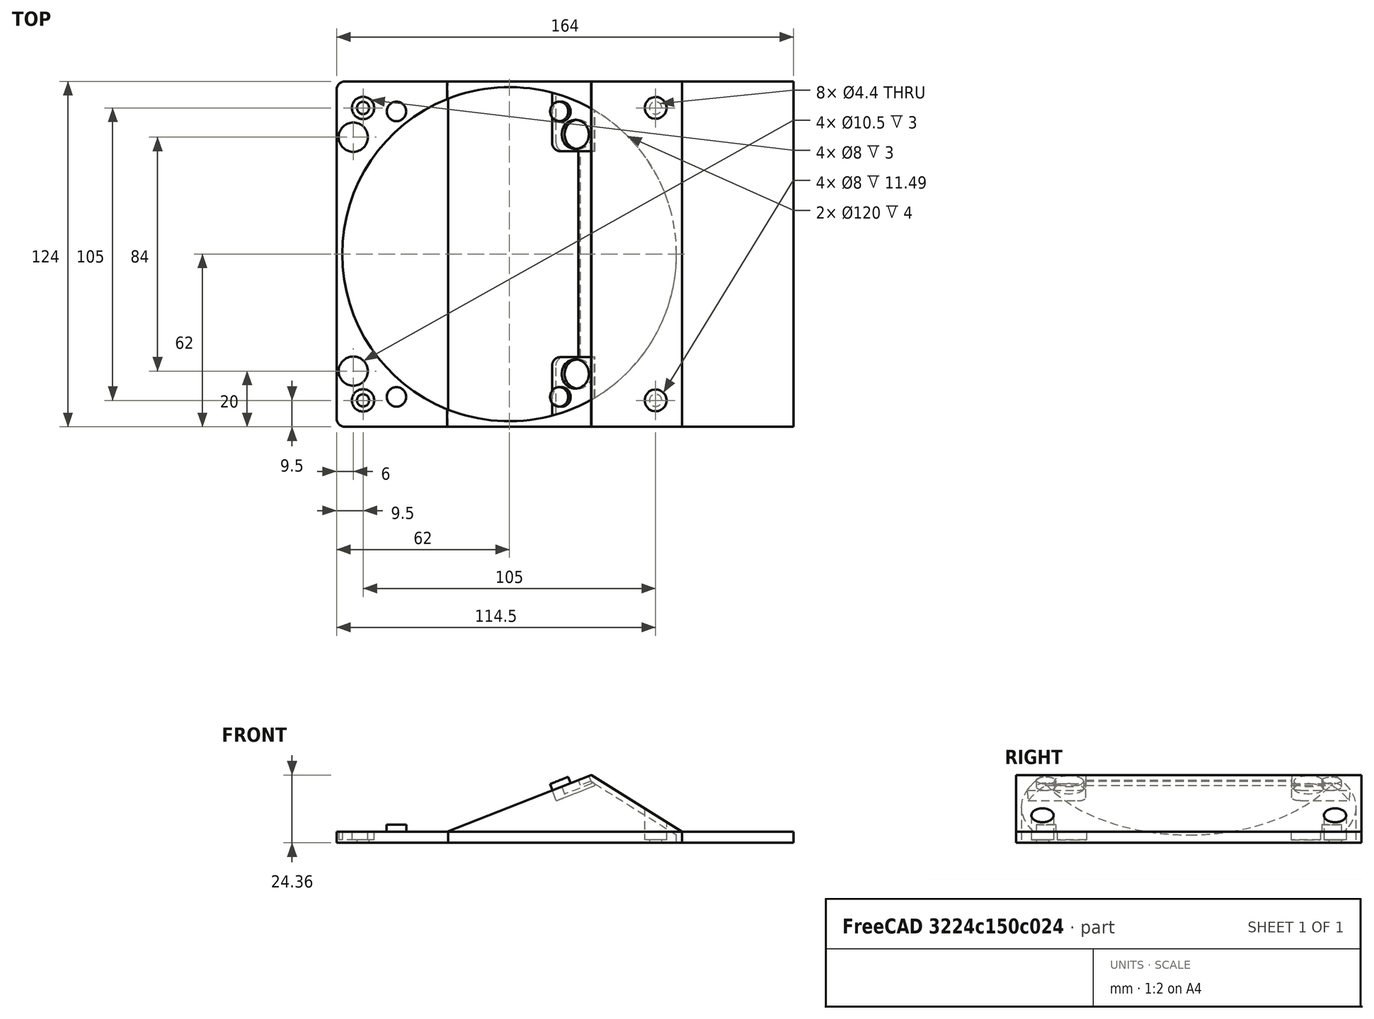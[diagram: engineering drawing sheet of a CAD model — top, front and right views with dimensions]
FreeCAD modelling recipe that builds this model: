
FCSTD DOCUMENT  (FreeCAD 0.20R29603 (Git))
Label: victron_fan_holder_mp2_8000
License: Creative Commons Attribution-NonCommercial-ShareAlike
LicenseURL: http://creativecommons.org/licenses/by-nc-sa/4.0/
objects: Part::Cylinder×39, Part::Cut×36, Part::Box×17, Part::MultiFuse×12, Part::Fillet×6
note: 110 computed .brp shape members not serialized (recipe doc carries the construction recipe); baked Part::Feature solids carry a one-line shape summary decoded from their .brp

FEATURE [Part::Cylinder] Cylinder
  Angle = 360
  AttacherType = Attacher::AttachEngine3D
  FirstAngle = 0
  Height = 4
  Placement = pos=(0,0,-4) rot=(0,0,1;0rad)
  Radius = 60
  SecondAngle = 0
FEATURE [Part::Box] Box  label="Cube"
  AttacherType = Attacher::AttachEngine3D
  Height = 4
  Length = 124
  Placement = pos=(-62,-62,-4) rot=(0,0,1;0rad)
  Width = 124
FEATURE [Part::Cylinder] Cylinder001  label="magnet_hole_1"
  Angle = 360
  AttacherType = Attacher::AttachEngine3D
  FirstAngle = 0
  Height = 3
  Placement = pos=(-56,-42,-3) rot=(0,0,1;0rad)
  Radius = 5.25
  SecondAngle = 0
FEATURE [Part::Cut] Cut
  Base = -> Box
  Tool = -> Cylinder
FEATURE [Part::Cylinder] Cylinder002  label="fan_hole_1"
  Angle = 360
  AttacherType = Attacher::AttachEngine3D
  FirstAngle = 0
  Height = 4
  Placement = pos=(-52.5,-52.5,-4) rot=(0,0,1;0rad)
  Radius = 2.2
  SecondAngle = 0
FEATURE [Part::Cylinder] Cylinder003  label="fan_hole_1_deepening"
  Angle = 360
  AttacherType = Attacher::AttachEngine3D
  FirstAngle = 0
  Height = 3
  Placement = pos=(-52.5,-52.5,-3) rot=(0,0,1;0rad)
  Radius = 4
  SecondAngle = 0
FEATURE [Part::Cylinder] Cylinder004  label="fan_hole_2_deepening"
  Angle = 360
  AttacherType = Attacher::AttachEngine3D
  FirstAngle = 0
  Height = 50
  Placement = pos=(52.5,-52.5,-3) rot=(0,0,1;0rad)
  Radius = 4
  SecondAngle = 0
FEATURE [Part::Cylinder] Cylinder005  label="fan_hole_2"
  Angle = 360
  AttacherType = Attacher::AttachEngine3D
  FirstAngle = 0
  Height = 50
  Placement = pos=(52.5,-52.5,-4) rot=(0,0,1;0rad)
  Radius = 2.2
  SecondAngle = 0
FEATURE [Part::Cylinder] Cylinder006  label="fan_hole_3_deepening"
  Angle = 360
  AttacherType = Attacher::AttachEngine3D
  FirstAngle = 0
  Height = 3
  Placement = pos=(-52.5,52.5,-3) rot=(0,0,1;0rad)
  Radius = 4
  SecondAngle = 0
FEATURE [Part::Cylinder] Cylinder007  label="fan_hole_3"
  Angle = 360
  AttacherType = Attacher::AttachEngine3D
  FirstAngle = 0
  Height = 4
  Placement = pos=(-52.5,52.5,-4) rot=(0,0,1;0rad)
  Radius = 2.2
  SecondAngle = 0
FEATURE [Part::Cylinder] Cylinder008  label="fan_hole_4_deepening"
  Angle = 360
  AttacherType = Attacher::AttachEngine3D
  FirstAngle = 0
  Height = 50
  Placement = pos=(52.5,52.5,-3) rot=(0,0,1;0rad)
  Radius = 4
  SecondAngle = 0
FEATURE [Part::Cylinder] Cylinder009  label="fan_hole_4"
  Angle = 360
  AttacherType = Attacher::AttachEngine3D
  FirstAngle = 0
  Height = 50
  Placement = pos=(52.5,52.5,-4) rot=(0,0,1;0rad)
  Radius = 2.2
  SecondAngle = 0
FEATURE [Part::Cylinder] Cylinder010  label="pin_1"
  Angle = 360
  AttacherType = Attacher::AttachEngine3D
  FirstAngle = 0
  Height = 2.5
  Placement = pos=(-40.5,-51.25,0) rot=(0,0,1;0rad)
  Radius = 3.5
  SecondAngle = 0
FEATURE [Part::Cylinder] Cylinder011  label="pin_2"
  Angle = 360
  AttacherType = Attacher::AttachEngine3D
  FirstAngle = 0
  Height = 2.5
  Placement = pos=(-40.5,51.25,0) rot=(0,0,1;0rad)
  Radius = 3.5
  SecondAngle = 0
FEATURE [Part::Box] Box002  label="Cube002"
  AttacherType = Attacher::AttachEngine3D
  Height = 50
  Length = 83
  Placement = pos=(-9,-62,-48.5) rot=(0,-1,0;0.375246rad)
  Width = 124
FEATURE [Part::Cylinder] Cylinder012  label="magnet_hole_2"
  Angle = 360
  AttacherType = Attacher::AttachEngine3D
  FirstAngle = 0
  Height = 3
  Placement = pos=(-56,42,-3) rot=(0,0,1;0rad)
  Radius = 5.25
  SecondAngle = 0
FEATURE [Part::Cylinder] Cylinder013
  Angle = 360
  AttacherType = Attacher::AttachEngine3D
  FirstAngle = 0
  Height = 100
  Placement = pos=(0,0,-4) rot=(0,0,1;0rad)
  Radius = 60
  SecondAngle = 0
FEATURE [Part::Box] Box003  label="Cube003"
  AttacherType = Attacher::AttachEngine3D
  Height = 4
  Length = 124
  Placement = pos=(-22,-62,-4) rot=(0,0,1;0rad)
  Width = 124
FEATURE [Part::Box] Box004  label="rear_slant"
  AttacherType = Attacher::AttachEngine3D
  Height = 2
  Length = 38.5
  Placement = pos=(28.3,-62,18.65) rot=(0,1,0;0.558505rad)
  Width = 124
FEATURE [Part::Cut] Cut001
  Base = -> Box002
  Tool = -> Cylinder013
FEATURE [Part::Box] Box007  label="Cube007"
  AttacherType = Attacher::AttachEngine3D
  Height = 100
  Length = 200
  Placement = pos=(-100,-100,-100) rot=(0,0,1;0rad)
  Width = 200
FEATURE [Part::Cut] Cut002
  Base = -> Cut001
  Tool = -> Box007
FEATURE [Part::Cylinder] Cylinder014  label="pin_003"
  Angle = 360
  AttacherType = Attacher::AttachEngine3D
  FirstAngle = 0
  Height = 2.5
  Placement = pos=(18.8026,-51.25,16.0727) rot=(0,-1,0;0.375246rad)
  Radius = 3.5
  SecondAngle = 0
FEATURE [Part::Box] Box008  label="pinholder_3"
  AttacherType = Attacher::AttachEngine3D
  Height = 4
  Length = 15
  Placement = pos=(16.8,-62,11.1) rot=(0,-1,0;0.375246rad)
  Width = 25
FEATURE [Part::Cylinder] Cylinder015  label="magnet_hole_003"
  Angle = 360
  AttacherType = Attacher::AttachEngine3D
  FirstAngle = 0
  Height = 3
  Placement = pos=(24.73,-43,15.4) rot=(0,-1,0;0.375246rad)
  Radius = 5.25
  SecondAngle = 0
FEATURE [Part::Box] Box009  label="pinholder_4"
  AttacherType = Attacher::AttachEngine3D
  Height = 4
  Length = 15
  Placement = pos=(16.8,37,11.1) rot=(0,-1,0;0.375246rad)
  Width = 25
FEATURE [Part::Cylinder] Cylinder016  label="pin_004"
  Angle = 360
  AttacherType = Attacher::AttachEngine3D
  FirstAngle = 0
  Height = 2.5
  Placement = pos=(18.8,51.25,16.07) rot=(0,-1,0;0.375246rad)
  Radius = 3.5
  SecondAngle = 0
FEATURE [Part::Fillet] Fillet
  Base = -> Cut
  Edges = 2 edges r=3: [Edge1,Edge3]
FEATURE [Part::Fillet] Fillet001
  Base = -> Box008
  Edges = 1 edges r=3: [Edge3]
FEATURE [Part::Fillet] Fillet002
  Base = -> Box009
  Edges = 1 edges r=3: [Edge1]
FEATURE [Part::MultiFuse] Fusion
  Shapes = -> [Fillet,Cylinder010,Cylinder011]
FEATURE [Part::Cut] Cut003
  Base = -> Fusion
  Tool = -> Cylinder001
FEATURE [Part::Cut] Cut004
  Base = -> Cut003
  Tool = -> Cylinder012
FEATURE [Part::Cut] Cut005
  Base = -> Cut004
  Tool = -> Cylinder002
FEATURE [Part::Cut] Cut006
  Base = -> Cut005
  Tool = -> Cylinder003
FEATURE [Part::Cut] Cut007
  Base = -> Cut006
  Tool = -> Cylinder006
FEATURE [Part::Cut] Cut008
  Base = -> Cut007
  Tool = -> Cylinder007
FEATURE [Part::MultiFuse] Fusion001
  Shapes = -> [Cut008,Cut002]
FEATURE [Part::Box] Box010  label="Cube010"
  AttacherType = Attacher::AttachEngine3D
  Height = 20
  Length = 57
  Placement = pos=(13,-62,30.5) rot=(0,1,0;0.558505rad)
  Width = 124
FEATURE [Part::Cut] Cut009
  Base = -> Fusion001
  Tool = -> Box010
FEATURE [Part::MultiFuse] Fusion002
  Shapes = -> [Cut009,Box004]
FEATURE [Part::MultiFuse] Fusion003
  Shapes = -> [Fusion002,Fillet002,Fillet001]
FEATURE [Part::MultiFuse] Fusion004
  Shapes = -> [Fusion003,Cylinder016,Cylinder014]
FEATURE [Part::Box] Box011  label="pinholder_004"
  AttacherType = Attacher::AttachEngine3D
  Height = 2
  Length = 5
  Placement = pos=(25.5042,-62,16.665) rot=(0,-1,0;0.375246rad)
  Width = 124
FEATURE [Part::Cylinder] Cylinder017  label="magnet_hole_004"
  Angle = 360
  AttacherType = Attacher::AttachEngine3D
  FirstAngle = 0
  Height = 3
  Placement = pos=(24.73,43,15.4) rot=(0,-1,0;0.375246rad)
  Radius = 5.25
  SecondAngle = 0
FEATURE [Part::Cut] Cut010
  Base = -> Fusion004
  Tool = -> Cylinder017
FEATURE [Part::Cut] Cut011
  Base = -> Cut010
  Tool = -> Cylinder015
FEATURE [Part::Cut] Cut012
  Base = -> Cut011
  Tool = -> Cylinder009
FEATURE [Part::Cut] Cut013
  Base = -> Cut012
  Tool = -> Cylinder008
FEATURE [Part::Cut] Cut014
  Base = -> Cut013
  Tool = -> Cylinder005
FEATURE [Part::Cut] Cut015
  Base = -> Cut014
  Tool = -> Cylinder004
FEATURE [Part::Cylinder] Cylinder018  label="magnet_hole_005"
  Angle = 360
  AttacherType = Attacher::AttachEngine3D
  FirstAngle = 0
  Height = 3
  Placement = pos=(24.73,-43,15.4) rot=(0,-1,0;0.375246rad)
  Radius = 5.25
  SecondAngle = 0
FEATURE [Part::Cut] Cut016
  Base = -> Box011
  Tool = -> Cylinder018
FEATURE [Part::Cylinder] Cylinder019  label="magnet_hole_006"
  Angle = 360
  AttacherType = Attacher::AttachEngine3D
  FirstAngle = 0
  Height = 3
  Placement = pos=(24.73,43,15.4) rot=(0,-1,0;0.375246rad)
  Radius = 5.25
  SecondAngle = 0
FEATURE [Part::Cut] Cut017
  Base = -> Cut016
  Tool = -> Cylinder019
FEATURE [Part::MultiFuse] Fusion005  label="fan_holder_l"
  Shapes = -> [Cut017,Cut015]
FEATURE [Part::Box] Box012  label="Cube011"
  AttacherType = Attacher::AttachEngine3D
  Height = 4
  Length = 124
  Placement = pos=(-62,-62,-4) rot=(0,0,1;0rad)
  Width = 124
FEATURE [Part::Box] Box013  label="Cube012"
  AttacherType = Attacher::AttachEngine3D
  Height = 50
  Length = 83
  Placement = pos=(-9,-62,-48.5) rot=(0,-1,0;0.375246rad)
  Width = 124
FEATURE [Part::Box] Box014  label="rear_slant001"
  AttacherType = Attacher::AttachEngine3D
  Height = 2
  Length = 38.5
  Placement = pos=(28.3,-62,18.65) rot=(0,1,0;0.558505rad)
  Width = 124
FEATURE [Part::Box] Box015  label="Cube013"
  AttacherType = Attacher::AttachEngine3D
  Height = 100
  Length = 200
  Placement = pos=(-100,-100,-100) rot=(0,0,1;0rad)
  Width = 200
FEATURE [Part::Box] Box016  label="pinholder_005"
  AttacherType = Attacher::AttachEngine3D
  Height = 4
  Length = 15
  Placement = pos=(16.8,-62,11.1) rot=(0,-1,0;0.375246rad)
  Width = 25
FEATURE [Part::Box] Box017  label="pinholder_006"
  AttacherType = Attacher::AttachEngine3D
  Height = 4
  Length = 15
  Placement = pos=(16.8,37,11.1) rot=(0,-1,0;0.375246rad)
  Width = 25
FEATURE [Part::Box] Box018  label="Cube014"
  AttacherType = Attacher::AttachEngine3D
  Height = 20
  Length = 57
  Placement = pos=(13,-62,30.5) rot=(0,1,0;0.558505rad)
  Width = 124
FEATURE [Part::Box] Box019  label="pinholder_007"
  AttacherType = Attacher::AttachEngine3D
  Height = 2
  Length = 5
  Placement = pos=(25.5042,-62,16.665) rot=(0,-1,0;0.375246rad)
  Width = 124
FEATURE [Part::Cylinder] Cylinder020
  Angle = 360
  AttacherType = Attacher::AttachEngine3D
  FirstAngle = 0
  Height = 4
  Placement = pos=(0,0,-4) rot=(0,0,1;0rad)
  Radius = 60
  SecondAngle = 0
FEATURE [Part::Cut] Cut018
  Base = -> Box012
  Tool = -> Cylinder020
FEATURE [Part::Cylinder] Cylinder021  label="magnet_hole_007"
  Angle = 360
  AttacherType = Attacher::AttachEngine3D
  FirstAngle = 0
  Height = 3
  Placement = pos=(-56,-42,-3) rot=(0,0,1;0rad)
  Radius = 5.25
  SecondAngle = 0
FEATURE [Part::Cylinder] Cylinder022  label="fan_hole_005"
  Angle = 360
  AttacherType = Attacher::AttachEngine3D
  FirstAngle = 0
  Height = 4
  Placement = pos=(-52.5,-52.5,-4) rot=(0,0,1;0rad)
  Radius = 2.2
  SecondAngle = 0
FEATURE [Part::Cylinder] Cylinder023  label="fan_hole_1_deepening001"
  Angle = 360
  AttacherType = Attacher::AttachEngine3D
  FirstAngle = 0
  Height = 3
  Placement = pos=(-52.5,-52.5,-3) rot=(0,0,1;0rad)
  Radius = 4
  SecondAngle = 0
FEATURE [Part::Cylinder] Cylinder024  label="fan_hole_2_deepening001"
  Angle = 360
  AttacherType = Attacher::AttachEngine3D
  FirstAngle = 0
  Height = 50
  Placement = pos=(52.5,-52.5,-3) rot=(0,0,1;0rad)
  Radius = 4
  SecondAngle = 0
FEATURE [Part::Cylinder] Cylinder025  label="fan_hole_006"
  Angle = 360
  AttacherType = Attacher::AttachEngine3D
  FirstAngle = 0
  Height = 50
  Placement = pos=(52.5,-52.5,-4) rot=(0,0,1;0rad)
  Radius = 2.2
  SecondAngle = 0
FEATURE [Part::Cylinder] Cylinder026  label="fan_hole_3_deepening001"
  Angle = 360
  AttacherType = Attacher::AttachEngine3D
  FirstAngle = 0
  Height = 3
  Placement = pos=(-52.5,52.5,-3) rot=(0,0,1;0rad)
  Radius = 4
  SecondAngle = 0
FEATURE [Part::Cylinder] Cylinder027  label="fan_hole_007"
  Angle = 360
  AttacherType = Attacher::AttachEngine3D
  FirstAngle = 0
  Height = 4
  Placement = pos=(-52.5,52.5,-4) rot=(0,0,1;0rad)
  Radius = 2.2
  SecondAngle = 0
FEATURE [Part::Cylinder] Cylinder028  label="fan_hole_4_deepening001"
  Angle = 360
  AttacherType = Attacher::AttachEngine3D
  FirstAngle = 0
  Height = 50
  Placement = pos=(52.5,52.5,-3) rot=(0,0,1;0rad)
  Radius = 4
  SecondAngle = 0
FEATURE [Part::Cylinder] Cylinder029  label="fan_hole_008"
  Angle = 360
  AttacherType = Attacher::AttachEngine3D
  FirstAngle = 0
  Height = 50
  Placement = pos=(52.5,52.5,-4) rot=(0,0,1;0rad)
  Radius = 2.2
  SecondAngle = 0
FEATURE [Part::Cylinder] Cylinder030  label="pin_005"
  Angle = 360
  AttacherType = Attacher::AttachEngine3D
  FirstAngle = 0
  Height = 2.5
  Placement = pos=(-40.5,-51.25,0) rot=(0,0,1;0rad)
  Radius = 3.5
  SecondAngle = 0
FEATURE [Part::Cylinder] Cylinder032  label="magnet_hole_008"
  Angle = 360
  AttacherType = Attacher::AttachEngine3D
  FirstAngle = 0
  Height = 3
  Placement = pos=(-56,42,-3) rot=(0,0,1;0rad)
  Radius = 5.25
  SecondAngle = 0
FEATURE [Part::Cylinder] Cylinder033
  Angle = 360
  AttacherType = Attacher::AttachEngine3D
  FirstAngle = 0
  Height = 100
  Placement = pos=(0,0,-4) rot=(0,0,1;0rad)
  Radius = 60
  SecondAngle = 0
FEATURE [Part::Cut] Cut019
  Base = -> Box013
  Tool = -> Cylinder033
FEATURE [Part::Cut] Cut020
  Base = -> Cut019
  Tool = -> Box015
FEATURE [Part::Cylinder] Cylinder034  label="pin_007"
  Angle = 360
  AttacherType = Attacher::AttachEngine3D
  FirstAngle = 0
  Height = 2.5
  Placement = pos=(18.8026,-51.25,16.0727) rot=(0,-1,0;0.375246rad)
  Radius = 3.5
  SecondAngle = 0
FEATURE [Part::Cylinder] Cylinder035  label="magnet_hole_009"
  Angle = 360
  AttacherType = Attacher::AttachEngine3D
  FirstAngle = 0
  Height = 3
  Placement = pos=(24.73,-43,15.4) rot=(0,-1,0;0.375246rad)
  Radius = 5.25
  SecondAngle = 0
FEATURE [Part::Cylinder] Cylinder036  label="pin_008"
  Angle = 360
  AttacherType = Attacher::AttachEngine3D
  FirstAngle = 0
  Height = 2.5
  Placement = pos=(18.8,51.25,16.07) rot=(0,-1,0;0.375246rad)
  Radius = 3.5
  SecondAngle = 0
FEATURE [Part::Cylinder] Cylinder037  label="magnet_hole_010"
  Angle = 360
  AttacherType = Attacher::AttachEngine3D
  FirstAngle = 0
  Height = 3
  Placement = pos=(24.73,43,15.4) rot=(0,-1,0;0.375246rad)
  Radius = 5.25
  SecondAngle = 0
FEATURE [Part::Cylinder] Cylinder038  label="magnet_hole_011"
  Angle = 360
  AttacherType = Attacher::AttachEngine3D
  FirstAngle = 0
  Height = 3
  Placement = pos=(24.73,-43,15.4) rot=(0,-1,0;0.375246rad)
  Radius = 5.25
  SecondAngle = 0
FEATURE [Part::Cut] Cut034
  Base = -> Box019
  Tool = -> Cylinder038
FEATURE [Part::Cylinder] Cylinder039  label="magnet_hole_012"
  Angle = 360
  AttacherType = Attacher::AttachEngine3D
  FirstAngle = 0
  Height = 3
  Placement = pos=(24.73,43,15.4) rot=(0,-1,0;0.375246rad)
  Radius = 5.25
  SecondAngle = 0
FEATURE [Part::Cut] Cut035
  Base = -> Cut034
  Tool = -> Cylinder039
FEATURE [Part::Fillet] Fillet003
  Base = -> Cut018
  Edges = 2 edges r=3: [Edge1,Edge3]
FEATURE [Part::Fillet] Fillet004
  Base = -> Box016
  Edges = 1 edges r=3: [Edge3]
FEATURE [Part::Fillet] Fillet005
  Base = -> Box017
  Edges = 1 edges r=3: [Edge1]
FEATURE [Part::MultiFuse] Fusion006
  Shapes = -> [Fillet003,Cylinder030]
FEATURE [Part::Cut] Cut021
  Base = -> Fusion006
  Tool = -> Cylinder021
FEATURE [Part::Cut] Cut022
  Base = -> Cut021
  Tool = -> Cylinder032
FEATURE [Part::Cut] Cut023
  Base = -> Cut022
  Tool = -> Cylinder022
FEATURE [Part::Cut] Cut024
  Base = -> Cut023
  Tool = -> Cylinder023
FEATURE [Part::Cut] Cut025
  Base = -> Cut024
  Tool = -> Cylinder026
FEATURE [Part::Cut] Cut026
  Base = -> Cut025
  Tool = -> Cylinder027
FEATURE [Part::MultiFuse] Fusion007
  Shapes = -> [Cut026,Cut020]
FEATURE [Part::Cut] Cut027
  Base = -> Fusion007
  Tool = -> Box018
FEATURE [Part::MultiFuse] Fusion008
  Shapes = -> [Cut027,Box014]
FEATURE [Part::MultiFuse] Fusion009
  Shapes = -> [Fusion008,Fillet005,Fillet004]
FEATURE [Part::MultiFuse] Fusion010
  Shapes = -> [Fusion009,Cylinder036,Cylinder034]
FEATURE [Part::Cut] Cut028
  Base = -> Fusion010
  Tool = -> Cylinder037
FEATURE [Part::Cut] Cut029
  Base = -> Cut028
  Tool = -> Cylinder035
FEATURE [Part::Cut] Cut030
  Base = -> Cut029
  Tool = -> Cylinder029
FEATURE [Part::Cut] Cut031
  Base = -> Cut030
  Tool = -> Cylinder028
FEATURE [Part::Cut] Cut032
  Base = -> Cut031
  Tool = -> Cylinder025
FEATURE [Part::Cut] Cut033
  Base = -> Cut032
  Tool = -> Cylinder024
FEATURE [Part::MultiFuse] Fusion011  label="fan_holder_r"
  Shapes = -> [Cut035,Cut033]
